# Revit family: Jandy Pool Heater CXI500-750
name_source: partatom
category: Mechanical Equipment
revit_build: Autodesk Revit 2016 (Build: 20150701_1515(x64)
units: mm (PartAtom-declared; Revit-internal decimal feet)

## family parameters
Always vertical = Yes
Cut with Voids When Loaded = No
OmniClass Number = 23.65.35.11.17
OmniClass Title = Thermodynamic Water Heaters
Part Type = Normal
Room Calculation Point = No
Round Connector Dimension = Use Radius
Shared = No
Work Plane-Based = No

## types (3) — shared parameters
# of Electrical Connections = 2
A_HEIGHT = 31 1/2"
C_DEPTH = 22 1/4"
D_horiz water conn height = 38"
Description = Pool Heater
E_horiz water conn offset from left = 20 1/4"
FUEL TYPE = NATURAL GAS
F_pump dist from left = 26 1/2"
Fuel Type = Natural or LP
GAS CONN SIZE = 1 1/4"
G_gas conn height = 29"
H_vertical water conn offset from left = 9 3/4"
K_water outlet offset from water inlet = 12 3/4"
L_top water conn height = 41 1/4"
M_water inlet offset from front = 9"
Manufacturer = Lochinvar
SES BIM Studio # = 18 0649 03
Voltage/Control = 24
Voltage/Heater = 120
Voltage/Pump = 120
WATER CONN SIZE = 2"
gas conn offset from front = 20"
gas conn radius = 5/8"
horiz water conn offset from vertical water conn = -10 1/2"
pump extrusion = 13 1/4"
water bypass adjustment = -12 3/4"
water conn radius = 1"
water inlet sweep adjustment = 7 1/4"
water inlet sweep adjustment 2 = -7 1/4"
water outlet offset from back = 21 3/4"
water outlet sweep adjustment = 19 1/4"
water outlet sweep adjustment 2 = 16 3/4"

## per-type parameters (varying)
| type | AIR INLET SIZE | B_WIDTH | GALLON CAPACITY | INPUT RATE (BTUH) | J_vent offset from right | Total Amps | VENT SIZE | air inlet radius | back clearance | front clearance | left clearance | right clearance | top clearance | vent radius |
| CXI500 | 6" | 45 1/2" | 1.7 | 500,000 | 7" | 12.1 | 6" | 3" | 3" | 30" | 24" | 3" | 3" | 3" |
| CXI650 | 8" | 56 3/4" | 1.9 | 650,000 | 8 1/2" | 14.6 | 8" | 4" | 12 3/4" | 22 3/4" | 46 3/4" | 29 1/4" | 13" | 4" |
| CXI750 | 8" | 64" | 2.0 | 750,000 | 8 1/2" | 14.6 | 8" | 4" | 12 3/4" | 22 3/4" | 46 3/4" | 29 1/4" | 13" | 4" |

note: column(s) folded — value = type name in every type: MODEL NO., Model

## geometry (parser evidence)
native form markers: Sweep x2
no freeform markers — native parametric forms only
